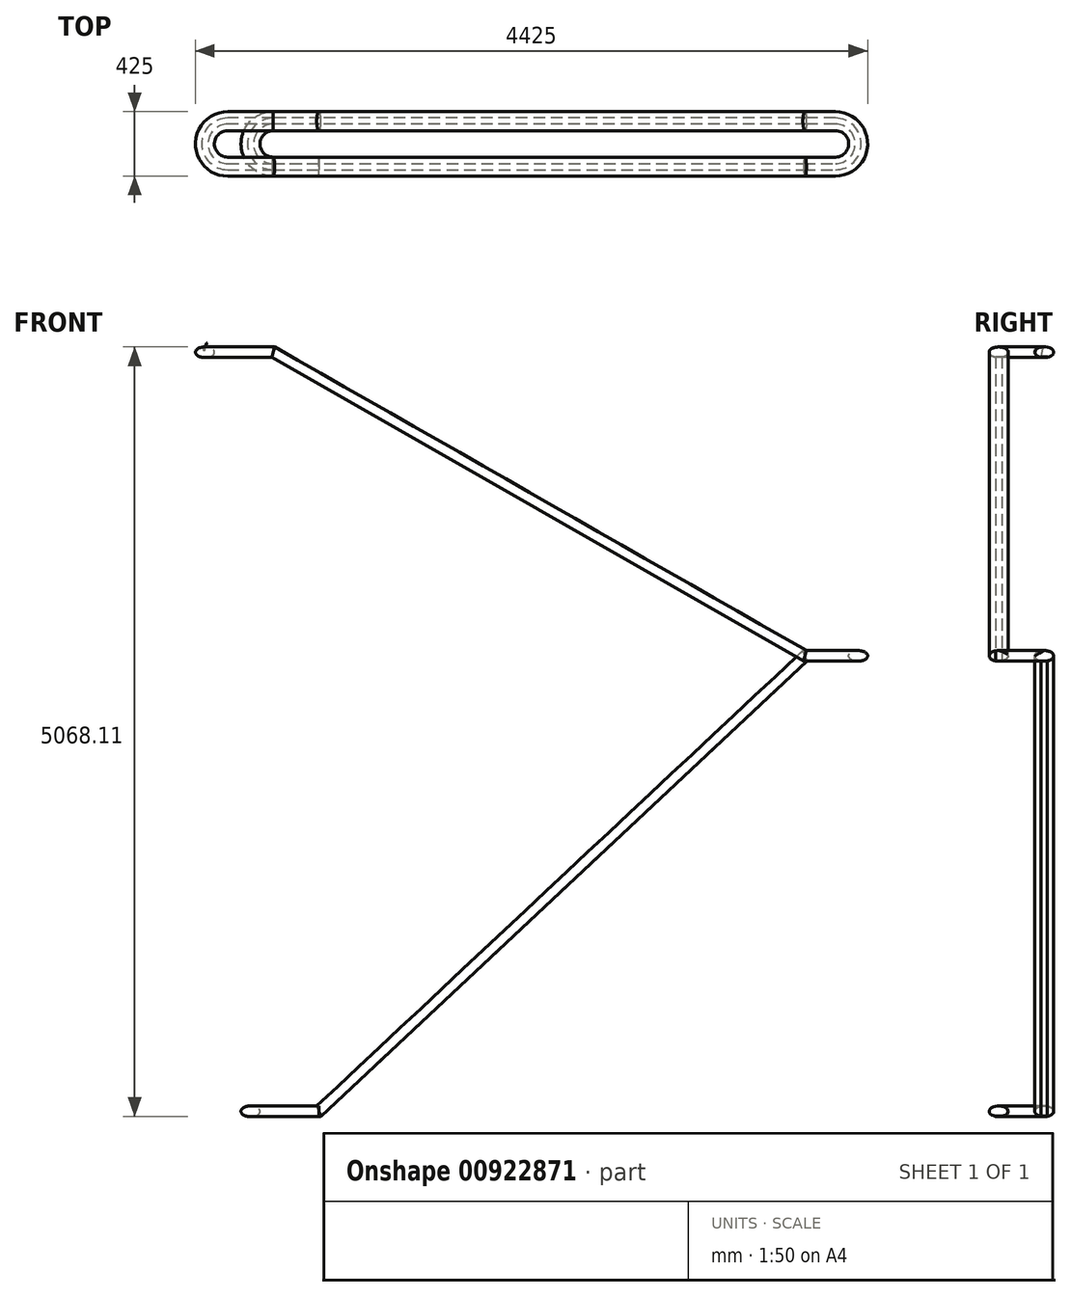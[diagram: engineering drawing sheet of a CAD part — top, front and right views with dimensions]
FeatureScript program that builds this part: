
annotation { "Feature Type Name" : "Feature", "Feature Type Description" : "" }
export const myFeature = defineFeature(function(context is Context, id is Id, definition is map)
    precondition{}
    {
        {
            var Q0;
            Q0=qCreatedBy(makeId("Top.planeOp"),FACE);
            cPlane(context, id + "F0", {"entities" : qUnion([Q0]), "cplaneType" : CPlaneType.OFFSET, "offset" : 1000 * mm, "width" : 150 * mm, "height" : 150 * mm});
        }
        {
            var Q0;
            Q0=qCreatedBy(id+"F0.planeOp",FACE);
            cPlane(context, id + "F1", {"entities" : qUnion([Q0]), "cplaneType" : CPlaneType.OFFSET, "offset" : 2000 * mm, "width" : 150 * mm, "height" : 150 * mm});
        }
        {
            var Q0;
            Q0=qCreatedBy(id+"F1.planeOp",FACE);
            cPlane(context, id + "F2", {"entities" : qUnion([Q0]), "cplaneType" : CPlaneType.OFFSET, "offset" : 2000 * mm, "width" : 150 * mm, "height" : 150 * mm});
        }
        {
            var Q0;
            Q0=qCreatedBy(makeId("Front.planeOp"),FACE);
            cPlane(context, id + "F3", {"entities" : qUnion([Q0]), "cplaneType" : CPlaneType.OFFSET, "offset" : 150 * mm, "width" : 150 * mm, "height" : 150 * mm});
        }
        {
            var Q0;
            Q0=qCreatedBy(makeId("Front.planeOp"),FACE);
            cPlane(context, id + "F4", {"entities" : qUnion([Q0]), "cplaneType" : CPlaneType.OFFSET, "offset" : 150 * mm, "oppositeDirection" : true, "width" : 150 * mm, "height" : 150 * mm});
        }
        {
            var Q0;
            Q0=qCreatedBy(makeId("Top.planeOp"),FACE);
            cPlane(context, id + "F5", {"entities" : qUnion([Q0]), "cplaneType" : CPlaneType.OFFSET, "offset" : 1100 * mm, "width" : 150 * mm, "height" : 150 * mm});
        }
        {
            var Q0;
            Q0=qCreatedBy(id+"F1.planeOp",FACE);
            cPlane(context, id + "F6", {"entities" : qUnion([Q0]), "cplaneType" : CPlaneType.OFFSET, "offset" : 1100 * mm, "width" : 150 * mm, "height" : 150 * mm});
        }
        {
            var Q0;
            Q0=qCreatedBy(id+"F6.planeOp",FACE);
            var sketch = newSketch(context, id + "F7", { "sketchPlane" : qUnion([Q0])});
            skArc(sketch, "E0", {"start": v(2200, -150) * mm, "mid": v(2350, 0) * mm, "end": v(2200, 150) * mm});
            skLineSegment(sketch, "E1", {"start": v(2200, 0) * mm, "end": v(1121.96, 0) * mm, "construction": true});
            skLineSegment(sketch, "E2.0", {"start": v(2200, 150) * mm, "end": v(2000, 150) * mm});
            skLineSegment(sketch, "E3.0", {"start": v(2200, -150) * mm, "end": v(2000, -150) * mm});
            skSolve(sketch);
        }
        {
            var Q0;
            Q0=qCreatedBy(id+"F5.planeOp",FACE);
            var sketch = newSketch(context, id + "F8", { "sketchPlane" : qUnion([Q0])});
            skArc(sketch, "E4", {"start": v(-1500, 150) * mm, "mid": v(-1650, 0) * mm, "end": v(-1500, -150) * mm});
            skLineSegment(sketch, "E5", {"start": v(-1500, 0) * mm, "end": v(2062.23, 0) * mm, "construction": true});
            skLineSegment(sketch, "E6.0", {"start": v(-1500, -150) * mm, "end": v(-1200, -150) * mm});
            skLineSegment(sketch, "E7.0", {"start": v(-1500, 150) * mm, "end": v(-1200, 150) * mm});
            skLineSegment(sketch, "E8", {"start": v(-1200, -150) * mm, "end": v(-1200, 150) * mm, "construction": true});
            skSolve(sketch);
        }
        {
            var Q0;
            Q0=qCreatedBy(id+"F4.planeOp",FACE);
            var sketch = newSketch(context, id + "F9", { "sketchPlane" : qUnion([Q0])});
            skLineSegment(sketch, "E9", {"start": v(-1200, 1100) * mm, "end": v(2000, 4100) * mm});
            skSolve(sketch);
        }
        {
            var Q0;
            Q0=qCreatedBy(id+"F2.planeOp",FACE);
            cPlane(context, id + "F10", {"entities" : qUnion([Q0]), "cplaneType" : CPlaneType.OFFSET, "offset" : 1100 * mm, "width" : 150 * mm, "height" : 150 * mm});
        }
        {
            var Q0;
            Q0=qCreatedBy(id+"F10.planeOp",FACE);
            var sketch = newSketch(context, id + "F11", { "sketchPlane" : qUnion([Q0])});
            skArc(sketch, "E10", {"start": v(-1800, 150) * mm, "mid": v(-1950, 0) * mm, "end": v(-1800, -150) * mm});
            skLineSegment(sketch, "E11", {"start": v(-1800, 0) * mm, "end": v(934.13, 0) * mm, "construction": true});
            skLineSegment(sketch, "E12.0", {"start": v(-1800, -150) * mm, "end": v(-1500, -150) * mm});
            skLineSegment(sketch, "E13.0", {"start": v(-1800, 150) * mm, "end": v(-1500, 150) * mm});
            skSolve(sketch);
        }
        {
            var Q0;
            Q0=qCreatedBy(id+"F3.planeOp",FACE);
            var sketch = newSketch(context, id + "F12", { "sketchPlane" : qUnion([Q0])});
            skLineSegment(sketch, "E14", {"start": v(-1500, 6100) * mm, "end": v(2000, 4100) * mm});
            skSolve(sketch);
        }
        {
            var Q0;
            Q0=qCreatedBy(makeId("Right.planeOp"),FACE);
            cPlane(context, id + "F13", {"entities" : qUnion([Q0]), "cplaneType" : CPlaneType.OFFSET, "offset" : 1350 * mm, "oppositeDirection" : true, "width" : 150 * mm, "height" : 150 * mm});
        }
        {
            var Q0;
            Q0=qCreatedBy(id+"F13.planeOp",FACE);
            var sketch = newSketch(context, id + "F14", { "sketchPlane" : qUnion([Q0])});
            skEllipticalArc(sketch, "E15", {});
            skLineSegment(sketch, "E16.0", {"start": v(-150, 1070) * mm, "end": v(-170.25, 1070) * mm});
            skLineSegment(sketch, "E17.0", {"start": v(-150, 1070) * mm, "end": v(-129.75, 1070) * mm});
            skLineSegment(sketch, "E18", {"start": v(-170.25, 1066.89) * mm, "end": v(-170.25, 1070) * mm});
            skLineSegment(sketch, "E19", {"start": v(-129.75, 1066.89) * mm, "end": v(-129.75, 1070) * mm});
            const initialGuessF14  = {"E15": [-0.15, 1.1, 1, 0, 0.0625, 0.035, 5.042343498213606, 4.382434462555773]};
            skSetInitialGuess(sketch, initialGuessF14);
            skSolve(sketch);
        }
        {
            var Q0;
            Q0 = qSketchRegion(id + "F14", true);
            var Q1;
            Q1=sQuery(id+"F8.wireOp",EDGE,"E6.0");
            var Q2;
            Q2=sQuery(id+"F8.wireOp",EDGE,"E4");
            var Q3;
            Q3=sQuery(id+"F8.wireOp",EDGE,"E7.0");
            var Q4;
            Q4=sQuery(id+"F9.wireOp",EDGE,"E9");
            var Q5;
            Q5=sQuery(id+"F7.wireOp",EDGE,"E2.0");
            var Q6;
            Q6=sQuery(id+"F7.wireOp",EDGE,"E0");
            var Q7;
            Q7=sQuery(id+"F7.wireOp",EDGE,"E3.0");
            var Q8;
            Q8=sQuery(id+"F12.wireOp",EDGE,"E14");
            var Q9;
            Q9=sQuery(id+"F11.wireOp",EDGE,"E12.0");
            var Q10;
            Q10=sQuery(id+"F11.wireOp",EDGE,"E10");
            var Q11;
            Q11=sQuery(id+"F11.wireOp",EDGE,"E13.0");
            sweep(context, id + "F15", {"profiles" : qUnion([Q0]), "path" : qUnion([Q1, Q2, Q3, Q4, Q5, Q6, Q7, Q8, Q9, Q10, Q11])});
        }
        {
            var Q0;
            Q0=qCreatedBy(makeId("Top.planeOp"),FACE);
            cPlane(context, id + "F16", {"entities" : qUnion([Q0]), "cplaneType" : CPlaneType.OFFSET, "offset" : 780.03 * mm, "oppositeDirection" : true, "width" : 150 * mm, "height" : 150 * mm});
        }
    });
